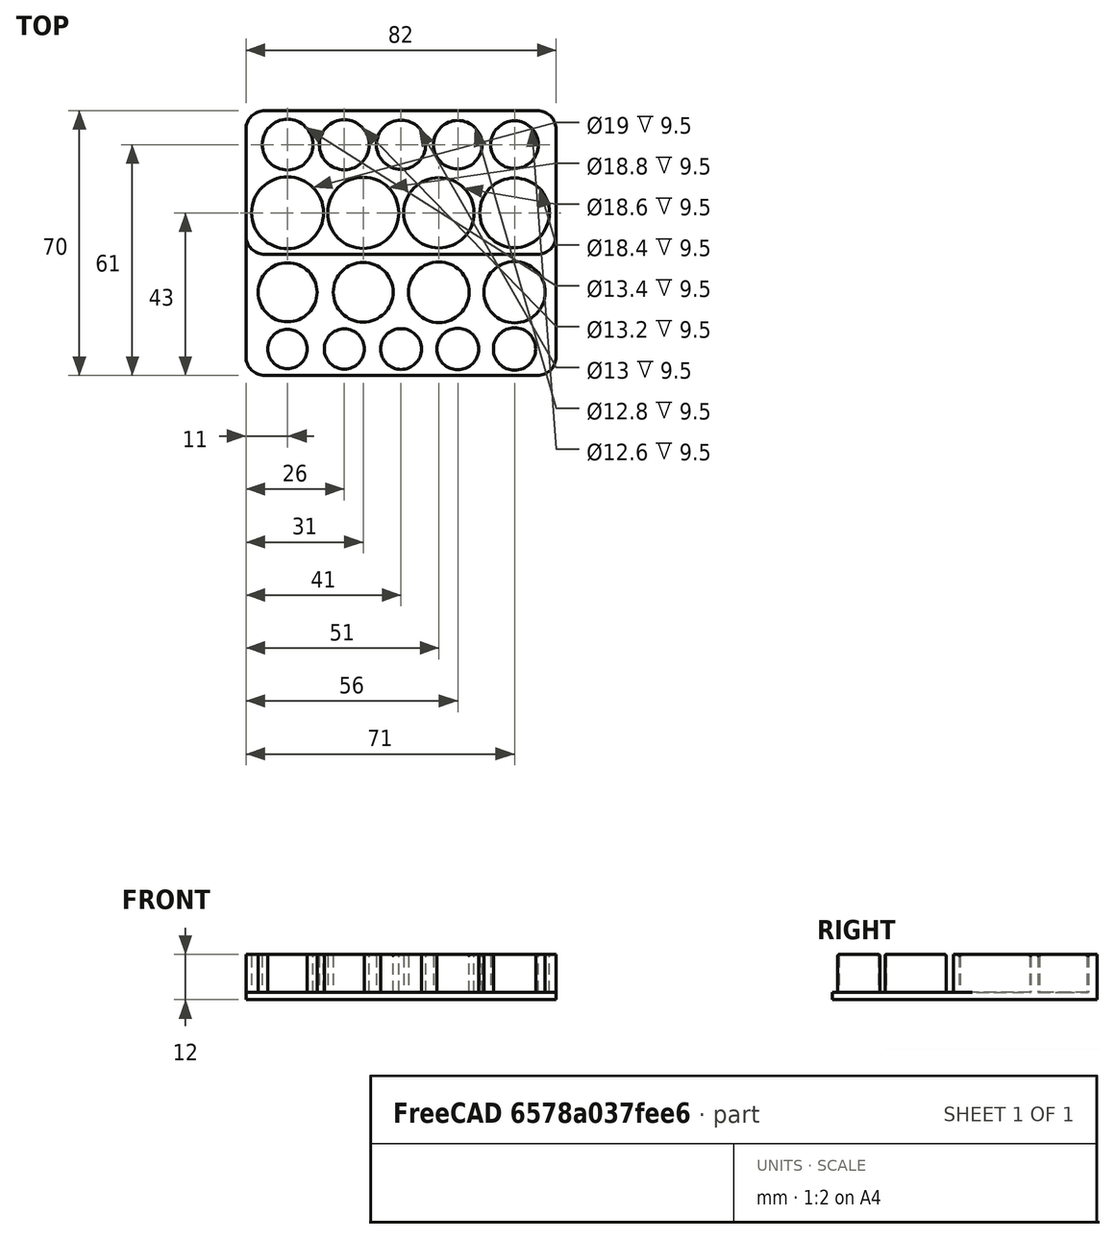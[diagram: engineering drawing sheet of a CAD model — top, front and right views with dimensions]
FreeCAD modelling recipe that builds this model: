
FCSTD DOCUMENT  (FreeCAD 0.20R29603 (Git))
Label: tube-socket-gauge
License: All rights reserved
LicenseURL: http://en.wikipedia.org/wiki/All_rights_reserved
objects: Part::Cylinder×18, Part::MultiFuse×8, Part::Fillet×3, Part::Box×2, Part::Cut×1
note: 32 computed .brp shape members not serialized (recipe doc carries the construction recipe); baked Part::Feature solids carry a one-line shape summary decoded from their .brp

FEATURE [Part::Cylinder] Cylinder  label="outer"
  Angle = 360
  AttacherType = Attacher::AttachEngine3D
  FirstAngle = 0
  Height = 10
  Radius = 9.5
  SecondAngle = 0
FEATURE [Part::Cylinder] Cylinder001  label="outer001"
  Angle = 360
  AttacherType = Attacher::AttachEngine3D
  FirstAngle = 0
  Height = 10
  Placement = pos=(20,0,0) rot=(0,0,1;0rad)
  Radius = 9.4
  SecondAngle = 0
FEATURE [Part::Cylinder] Cylinder002  label="outer002"
  Angle = 360
  AttacherType = Attacher::AttachEngine3D
  FirstAngle = 0
  Height = 10
  Placement = pos=(40,0,0) rot=(0,0,1;0rad)
  Radius = 9.3
  SecondAngle = 0
FEATURE [Part::Cylinder] Cylinder003  label="outer003"
  Angle = 360
  AttacherType = Attacher::AttachEngine3D
  FirstAngle = 0
  Height = 10
  Placement = pos=(60,0,0) rot=(0,0,1;0rad)
  Radius = 9.2
  SecondAngle = 0
FEATURE [Part::Cylinder] Cylinder004  label="outer004"
  Angle = 360
  AttacherType = Attacher::AttachEngine3D
  FirstAngle = 0
  Height = 10
  Placement = pos=(0,18,0) rot=(0,0,1;0rad)
  Radius = 6.7
  SecondAngle = 0
FEATURE [Part::Cylinder] Cylinder005  label="outer005"
  Angle = 360
  AttacherType = Attacher::AttachEngine3D
  FirstAngle = 0
  Height = 10
  Placement = pos=(15,18,0) rot=(0,0,1;0rad)
  Radius = 6.6
  SecondAngle = 0
FEATURE [Part::Cylinder] Cylinder006  label="outer006"
  Angle = 360
  AttacherType = Attacher::AttachEngine3D
  FirstAngle = 0
  Height = 10
  Placement = pos=(30,18,0) rot=(0,0,1;0rad)
  Radius = 6.5
  SecondAngle = 0
FEATURE [Part::Cylinder] Cylinder007  label="outer007"
  Angle = 360
  AttacherType = Attacher::AttachEngine3D
  FirstAngle = 0
  Height = 10
  Placement = pos=(45,18,0) rot=(0,0,1;0rad)
  Radius = 6.4
  SecondAngle = 0
FEATURE [Part::Cylinder] Cylinder008  label="outer008"
  Angle = 360
  AttacherType = Attacher::AttachEngine3D
  FirstAngle = 0
  Height = 10
  Placement = pos=(60,18,0) rot=(0,0,1;0rad)
  Radius = 6.3
  SecondAngle = 0
FEATURE [Part::MultiFuse] Fusion  label="outerrow1"
  Shapes = -> [Cylinder,Cylinder001,Cylinder002,Cylinder003]
FEATURE [Part::MultiFuse] Fusion001  label="outerrow2"
  Shapes = -> [Cylinder004,Cylinder005,Cylinder006,Cylinder007,Cylinder008]
FEATURE [Part::MultiFuse] Fusion002  label="outers"
  Shapes = -> [Fusion,Fusion001]
FEATURE [Part::Cylinder] Cylinder010  label="inner"
  Angle = 360
  AttacherType = Attacher::AttachEngine3D
  FirstAngle = 0
  Height = 10
  Placement = pos=(0,-21,0) rot=(0,0,1;0rad)
  Radius = 7.8
  SecondAngle = 0
FEATURE [Part::Cylinder] Cylinder011  label="inner001"
  Angle = 360
  AttacherType = Attacher::AttachEngine3D
  FirstAngle = 0
  Height = 10
  Placement = pos=(20,-21,0) rot=(0,0,1;0rad)
  Radius = 7.9
  SecondAngle = 0
FEATURE [Part::Cylinder] Cylinder012  label="inner002"
  Angle = 360
  AttacherType = Attacher::AttachEngine3D
  FirstAngle = 0
  Height = 10
  Placement = pos=(40,-21,0) rot=(0,0,1;0rad)
  Radius = 8
  SecondAngle = 0
FEATURE [Part::Cylinder] Cylinder013  label="inner003"
  Angle = 360
  AttacherType = Attacher::AttachEngine3D
  FirstAngle = 0
  Height = 10
  Placement = pos=(60,-21,0) rot=(0,0,1;0rad)
  Radius = 8.1
  SecondAngle = 0
FEATURE [Part::Cylinder] Cylinder014  label="inner004"
  Angle = 360
  AttacherType = Attacher::AttachEngine3D
  FirstAngle = 0
  Height = 10
  Placement = pos=(0,-36,0) rot=(0,0,1;0rad)
  Radius = 5.2
  SecondAngle = 0
FEATURE [Part::Cylinder] Cylinder015  label="inner005"
  Angle = 360
  AttacherType = Attacher::AttachEngine3D
  FirstAngle = 0
  Height = 10
  Placement = pos=(15,-36,0) rot=(0,0,1;0rad)
  Radius = 5.3
  SecondAngle = 0
FEATURE [Part::Cylinder] Cylinder016  label="inner006"
  Angle = 360
  AttacherType = Attacher::AttachEngine3D
  FirstAngle = 0
  Height = 10
  Placement = pos=(30,-36,0) rot=(0,0,1;0rad)
  Radius = 5.4
  SecondAngle = 0
FEATURE [Part::Cylinder] Cylinder017  label="inner007"
  Angle = 360
  AttacherType = Attacher::AttachEngine3D
  FirstAngle = 0
  Height = 10
  Placement = pos=(45,-36,0) rot=(0,0,1;0rad)
  Radius = 5.5
  SecondAngle = 0
FEATURE [Part::Cylinder] Cylinder018  label="inner008"
  Angle = 360
  AttacherType = Attacher::AttachEngine3D
  FirstAngle = 0
  Height = 10
  Placement = pos=(60,-36,0) rot=(0,0,1;0rad)
  Radius = 5.6
  SecondAngle = 0
FEATURE [Part::MultiFuse] Fusion003  label="innerrow1"
  Shapes = -> [Cylinder010,Cylinder011,Cylinder012,Cylinder013]
FEATURE [Part::MultiFuse] Fusion004  label="innerrow2"
  Shapes = -> [Cylinder014,Cylinder015,Cylinder016,Cylinder017,Cylinder018]
FEATURE [Part::MultiFuse] Fusion005  label="inners"
  Shapes = -> [Fusion003,Fusion004]
FEATURE [Part::Box] Box  label="bottom-plate"
  AttacherType = Attacher::AttachEngine3D
  Height = 2
  Length = 82
  Placement = pos=(-11,-43,-2) rot=(0,0,1;0rad)
  Width = 70
FEATURE [Part::Box] Box001  label="cutout-block"
  AttacherType = Attacher::AttachEngine3D
  Height = 10
  Length = 82
  Placement = pos=(-11,-11,0) rot=(0,0,1;0rad)
  Width = 38
FEATURE [Part::Fillet] Fillet
  Base = -> Box001
  Edges = 4 edges r=5: [Edge1,Edge3,Edge5,Edge7]
FEATURE [Part::Fillet] Fillet001
  Base = -> Box
  Edges = 4 edges r=5: [Edge1,Edge3,Edge5,Edge7]
FEATURE [Part::MultiFuse] Fusion006  label="rounded-main-block"
  Shapes = -> [Fillet,Fillet001]
FEATURE [Part::Cut] Cut
  Base = -> Fusion006
  Tool = -> Fusion002
FEATURE [Part::MultiFuse] Fusion007  label="finished-test-block"
  Shapes = -> [Fusion005,Cut]
FEATURE [Part::Fillet] Fillet002  label="rounded-edges"
  Base = -> Fusion007
  Edges = 18 edges r=0.5: [Edge12,Edge13,Edge14,Edge15,Edge16,Edge17,Edge18,Edge19,Edge20,Edge83,Edge85,Edge87,Edge89,Edge91,Edge93,Edge95,Edge97,Edge99]
